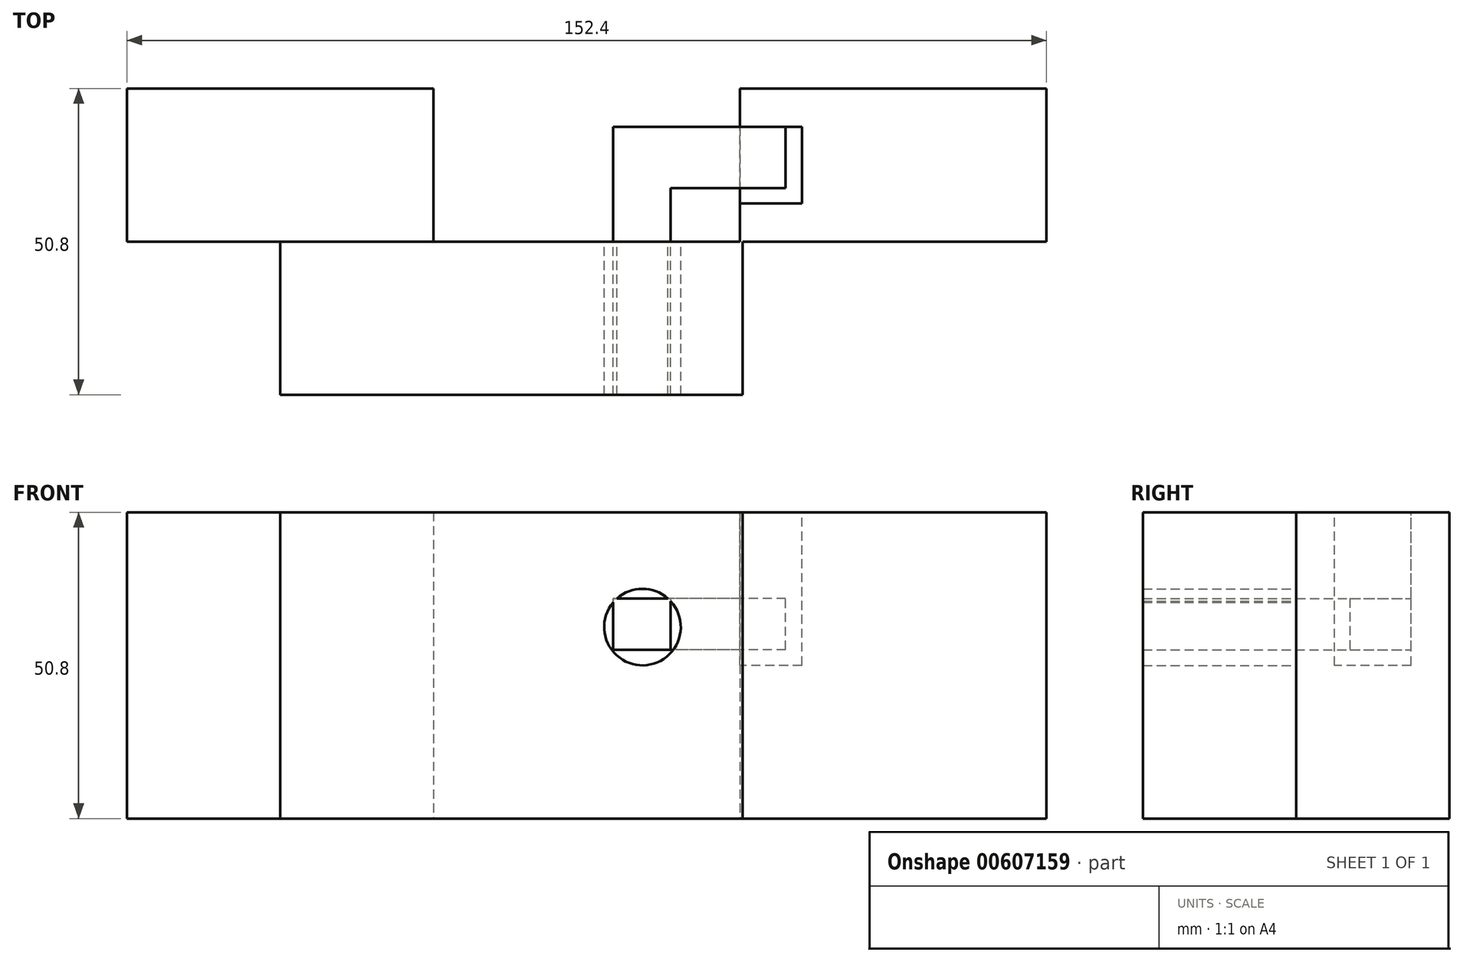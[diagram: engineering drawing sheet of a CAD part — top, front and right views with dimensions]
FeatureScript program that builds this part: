
annotation { "Feature Type Name" : "Feature", "Feature Type Description" : "" }
export const myFeature = defineFeature(function(context is Context, id is Id, definition is map)
    precondition{}
    {
        {
            var Q0;
            Q0=qCreatedBy(makeId("Front.planeOp"),FACE);
            var sketch = newSketch(context, id + "F0", { "sketchPlane" : qUnion([Q0])});
            skLineSegment(sketch, "E0.bottom", {"start": v(-69.83, 50.8) * mm, "end": v(-19.03, 50.8) * mm});
            skLineSegment(sketch, "E0.top", {"start": v(-69.83, 0) * mm, "end": v(-19.03, 0) * mm});
            skLineSegment(sketch, "E0.left", {"start": v(-69.83, 50.8) * mm, "end": v(-69.83, 0) * mm});
            skLineSegment(sketch, "E0.right", {"start": v(-19.03, 50.8) * mm, "end": v(-19.03, 0) * mm});
            skLineSegment(sketch, "E1", {"start": v(-19.03, 50.8) * mm, "end": v(31.77, 50.8) * mm});
            skLineSegment(sketch, "E2.bottom", {"start": v(31.77, 50.8) * mm, "end": v(82.57, 50.8) * mm});
            skLineSegment(sketch, "E2.top", {"start": v(31.77, 0) * mm, "end": v(82.57, 0) * mm});
            skLineSegment(sketch, "E2.left", {"start": v(31.77, 50.8) * mm, "end": v(31.77, 0) * mm});
            skLineSegment(sketch, "E2.right", {"start": v(82.57, 50.8) * mm, "end": v(82.57, 0) * mm});
            skSolve(sketch);
        }
        {
            var Q0;
            Q0 = qSketchRegion(id + "F0", true);
            extrude(context, id + "F1", {"entities" : qUnion([Q0]), "depth" : 25.4 * mm, "offsetDistance" : 25.4 * mm});
        }
        {
            var Q0;
            Q0=makeQuery(id+"F1.opExtrude","CAP_FACE",FACE,{"disambiguationData":[OSD([sQuery(id+"F0.wireOp",EDGE,"E0.bottom"),sQuery(id+"F0.wireOp",EDGE,"E0.top"),sQuery(id+"F0.wireOp",EDGE,"E0.left"),sQuery(id+"F0.wireOp",EDGE,"E0.right")])],"isStart":false});
            var sketch = newSketch(context, id + "F2", { "sketchPlane" : qUnion([Q0])});
            skLineSegment(sketch, "E3.bottom", {"start": v(-44.43, 50.8) * mm, "end": v(32.2, 50.8) * mm});
            skLineSegment(sketch, "E3.top", {"start": v(-44.43, 0) * mm, "end": v(32.2, 0) * mm});
            skLineSegment(sketch, "E3.left", {"start": v(-44.43, 50.8) * mm, "end": v(-44.43, 0) * mm});
            skLineSegment(sketch, "E3.right", {"start": v(32.2, 50.8) * mm, "end": v(32.2, 0) * mm});
            skSolve(sketch);
        }
        {
            var Q0;
            Q0 = qSketchRegion(id + "F2", true);
            extrude(context, id + "F3", {"entities" : qUnion([Q0]), "depth" : 25.4 * mm, "offsetDistance" : 25.4 * mm});
        }
        {
            var Q0;
            Q0=makeQuery(id+"F3.opExtrude","CAP_FACE",FACE,{"disambiguationData":[OSD([sQuery(id+"F2.wireOp",EDGE,"E3.bottom"),sQuery(id+"F2.wireOp",EDGE,"E3.top"),sQuery(id+"F2.wireOp",EDGE,"E3.left"),sQuery(id+"F2.wireOp",EDGE,"E3.right")])],"isStart":true});
            var sketch = newSketch(context, id + "F4", { "sketchPlane" : qUnion([Q0])});
            skCircle(sketch, "E4", {"center": v(-15.62, 31.75) * mm, "radius": 6.35 * mm});
            skSolve(sketch);
        }
        {
            var Q0;
            Q0 = qSketchRegion(id + "F4", true);
            extrude(context, id + "F5", {"entities" : qUnion([Q0]), "operationType" : NewBodyOperationType.REMOVE, "oppositeDirection" : true, "depth" : 25.4 * mm, "offsetDistance" : 25.4 * mm});
        }
        {
            var Q0;
            Q0=makeQuery(id+"F1.opExtrude","SWEPT_FACE",FACE,{"disambiguationData":[OSD([sQuery(id+"F0.wireOp",EDGE,"E2.left")])]});
            var sketch = newSketch(context, id + "F6", { "sketchPlane" : qUnion([Q0])});
            skLineSegment(sketch, "E5", {"start": v(0, 25.4) * mm, "end": v(6.35, 25.4) * mm});
            skLineSegment(sketch, "E6", {"start": v(25.4, 42.46) * mm, "end": v(19.05, 42.46) * mm});
            skLineSegment(sketch, "E7.bottom", {"start": v(6.35, 25.4) * mm, "end": v(19.05, 25.4) * mm});
            skLineSegment(sketch, "E7.top", {"start": v(6.35, 50.8) * mm, "end": v(19.05, 50.8) * mm});
            skLineSegment(sketch, "E7.left", {"start": v(6.35, 25.4) * mm, "end": v(6.35, 50.8) * mm});
            skLineSegment(sketch, "E7.right", {"start": v(19.05, 25.4) * mm, "end": v(19.05, 50.8) * mm});
            skSolve(sketch);
        }
        {
            var Q0;
            Q0 = qSketchRegion(id + "F6", true);
            extrude(context, id + "F7", {"entities" : qUnion([Q0]), "operationType" : NewBodyOperationType.REMOVE, "oppositeDirection" : true, "depth" : 10.29 * mm, "offsetDistance" : 25.4 * mm});
        }
        {
            var Q0;
            Q0=makeQuery(id+"F4.imprint","IMPRINT",FACE,{"disambiguationData":[TD([[makeQuery(id+"F4.imprint","IMPRINT",EDGE,{"derivedFrom":sQuery(id+"F4.wireOp",EDGE,"E4")}),1.0]])]});
            var sketch = newSketch(context, id + "F8", { "sketchPlane" : qUnion([Q0])});
            skLineSegment(sketch, "E8.bottom", {"start": v(-20.3, 28) * mm, "end": v(-10.77, 28) * mm});
            skLineSegment(sketch, "E8.top", {"start": v(-20.3, 36.5) * mm, "end": v(-10.77, 36.5) * mm});
            skLineSegment(sketch, "E8.left", {"start": v(-20.3, 28) * mm, "end": v(-20.3, 36.5) * mm});
            skLineSegment(sketch, "E8.right", {"start": v(-10.77, 28) * mm, "end": v(-10.77, 36.5) * mm});
            skSolve(sketch);
        }
        {
            var Q0;
            Q0 = qSketchRegion(id + "F8", true);
            extrude(context, id + "F9", {"entities" : qUnion([Q0]), "operationType" : NewBodyOperationType.ADD, "oppositeDirection" : true, "depth" : 25.4 * mm, "offsetDistance" : 25.4 * mm, "hasSecondDirection" : true, "secondDirectionOppositeDirection" : false, "secondDirectionDepth" : 19.05 * mm});
        }
        {
            var Q0;
            Q0=makeQuery(id+"F9.opExtrude","SWEPT_FACE",FACE,{"disambiguationData":[OSD([sQuery(id+"F8.wireOp",EDGE,"E8.left")])]});
            var sketch = newSketch(context, id + "F10", { "sketchPlane" : qUnion([Q0])});
            skLineSegment(sketch, "E9.bottom", {"start": v(-6.35, 36.5) * mm, "end": v(-16.51, 36.5) * mm});
            skLineSegment(sketch, "E9.top", {"start": v(-6.35, 28) * mm, "end": v(-16.51, 28) * mm});
            skLineSegment(sketch, "E9.left", {"start": v(-6.35, 36.5) * mm, "end": v(-6.35, 28) * mm});
            skLineSegment(sketch, "E9.right", {"start": v(-16.51, 36.5) * mm, "end": v(-16.51, 28) * mm});
            skSolve(sketch);
        }
        {
            var Q0;
            Q0=makeQuery(id+"F10.imprint","IMPRINT",FACE,{"disambiguationData":[TD([[makeQuery(id+"F10.imprint","IMPRINT",EDGE,{"derivedFrom":sQuery(id+"F10.wireOp",EDGE,"E9.bottom")}),-1.0]])]});
            extrude(context, id + "F11", {"entities" : qUnion([Q0]), "operationType" : NewBodyOperationType.ADD, "depth" : 19.05 * mm, "offsetDistance" : 25.4 * mm});
        }
    });
